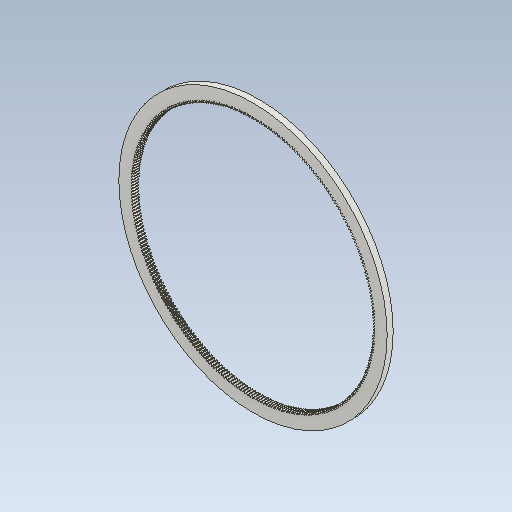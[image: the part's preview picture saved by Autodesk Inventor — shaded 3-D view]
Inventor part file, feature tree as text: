
AUTODESK INVENTOR PART (.ipt)
format: ipt  version: 2021 (Build 250183000, 183)  size: 1,325,568 bytes
history: native  units: mm (DEFAULTED — no unit token found)
features: plane x3, other x3, sketch x2, extrude x1
ambient origin geometry x8: Origin, YZ Plane, XZ Plane, XY Plane, X Axis, Y Axis, Z Axis, Center Point
bodies: Solid1 (feature_tree)
feature tree (9):
  extrude  "Extrusion1"  Depth=20.0mm TaperAngle=0.0deg
  plane  "Work Plane2"
  plane  "Work Plane8"
  plane  "Work Plane9"
  other  "Цилиндрическое зубчатое зацепление"
  sketch  "Sketch1"  dims[d0=887.038248mm d1=20.0mm d2=0.0mm]
  sketch  "Sketch2"  dims[d3=797.5mm d4=10.0mm d5=0.0mm d16=320.0mm d17=0.0mm d34=0.108331mm d39=0.0mm d45=0.0mm d47=320.0mm d50=0.0mm d51=0.0mm d52=320.0mm]
  other  "Srf1"
  other  "Средний диаметр"
